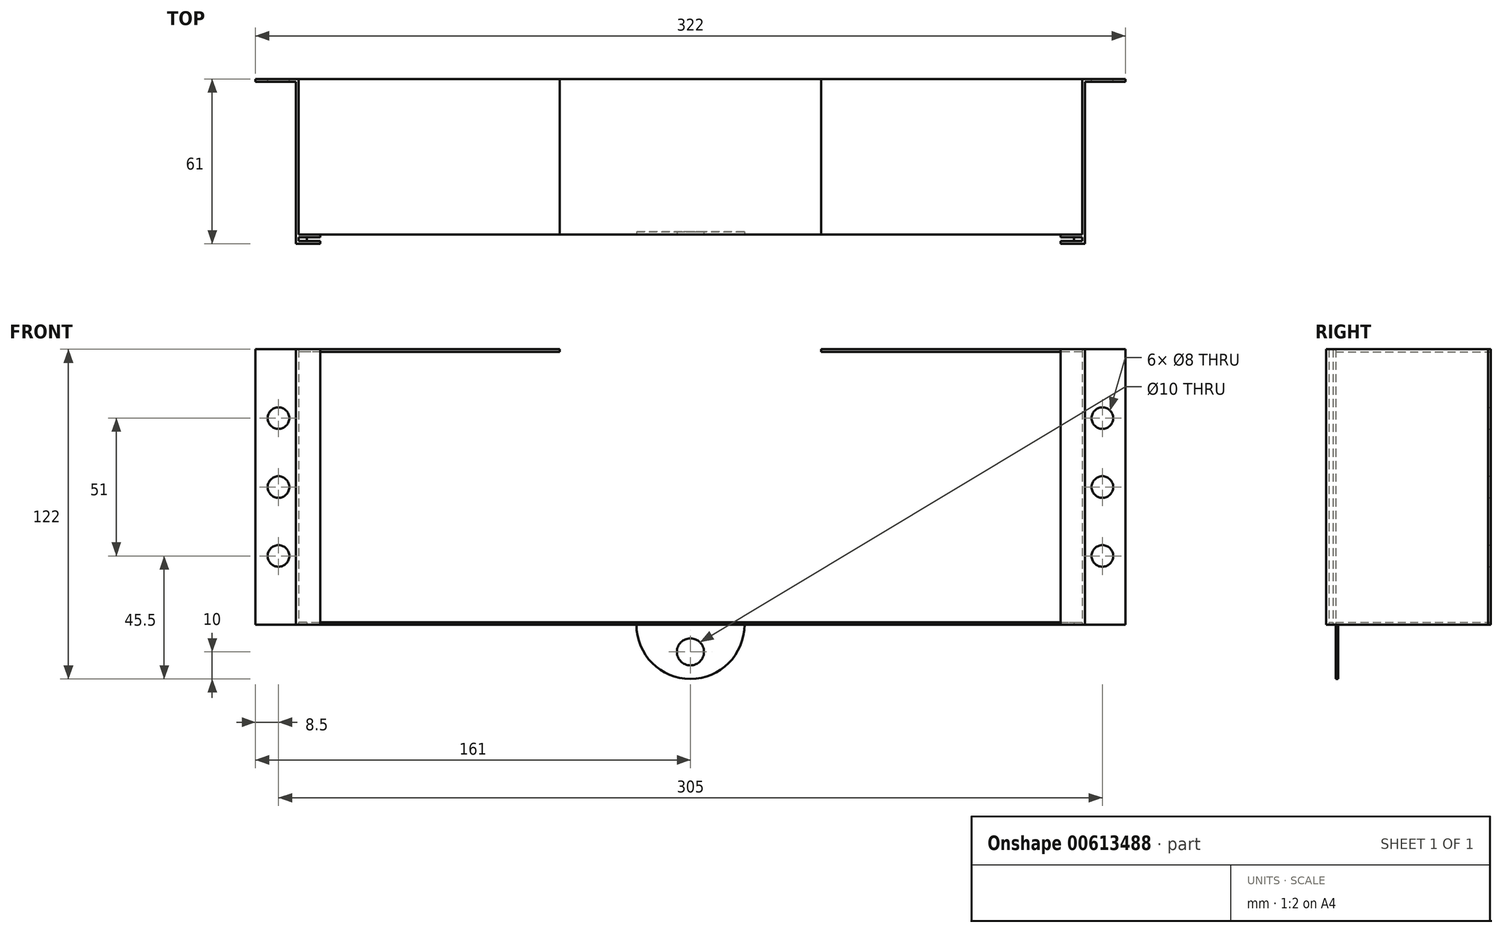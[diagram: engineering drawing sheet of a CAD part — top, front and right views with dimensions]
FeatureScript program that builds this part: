
annotation { "Feature Type Name" : "Feature", "Feature Type Description" : "" }
export const myFeature = defineFeature(function(context is Context, id is Id, definition is map)
    precondition{}
    {
        {
            var Q0;
            Q0=qCreatedBy(makeId("Top.planeOp"),FACE);
            var sketch = newSketch(context, id + "F0", { "sketchPlane" : qUnion([Q0])});
            skLineSegment(sketch, "E0", {"start": v(-146, 0) * mm, "end": v(-146, 60) * mm});
            skLineSegment(sketch, "E1", {"start": v(-146, 60) * mm, "end": v(-161, 60) * mm});
            skLineSegment(sketch, "E2", {"start": v(-161, 60) * mm, "end": v(-161, 61) * mm});
            skLineSegment(sketch, "E3", {"start": v(-161, 61) * mm, "end": v(-145, 61) * mm});
            skLineSegment(sketch, "E4", {"start": v(-145, 61) * mm, "end": v(-145, 3.5) * mm});
            skLineSegment(sketch, "E5", {"start": v(-145, 3.5) * mm, "end": v(-137, 3.5) * mm});
            skLineSegment(sketch, "E6", {"start": v(-137, 3.5) * mm, "end": v(-137, 2.5) * mm});
            skLineSegment(sketch, "E7", {"start": v(-137, 2.5) * mm, "end": v(-145, 2.5) * mm});
            skLineSegment(sketch, "E8", {"start": v(-146, 0) * mm, "end": v(-137, 0) * mm});
            skLineSegment(sketch, "E9", {"start": v(-137, 0) * mm, "end": v(-137, 1) * mm});
            skLineSegment(sketch, "E10", {"start": v(-137, 1) * mm, "end": v(-145, 1) * mm});
            skLineSegment(sketch, "E11", {"start": v(-145, 2.5) * mm, "end": v(-145, 1) * mm});
            skLineSegment(sketch, "E12.MirrorCS", {"start": v(137, 0) * mm, "end": v(137, 1) * mm});
            skLineSegment(sketch, "E13.MirrorCS", {"start": v(137, 3.5) * mm, "end": v(137, 2.5) * mm});
            skLineSegment(sketch, "E14.MirrorCS", {"start": v(145, 2.5) * mm, "end": v(145, 1) * mm});
            skLineSegment(sketch, "E15.MirrorCS", {"start": v(161, 60) * mm, "end": v(161, 61) * mm});
            skLineSegment(sketch, "E16.MirrorCS", {"start": v(146, 0) * mm, "end": v(146, 60) * mm});
            skLineSegment(sketch, "E17.MirrorCS", {"start": v(146, 60) * mm, "end": v(161, 60) * mm});
            skLineSegment(sketch, "E18.MirrorCS", {"start": v(146, 0) * mm, "end": v(137, 0) * mm});
            skLineSegment(sketch, "E19.MirrorCS", {"start": v(145, 3.5) * mm, "end": v(137, 3.5) * mm});
            skLineSegment(sketch, "E20.MirrorCS", {"start": v(145, 61) * mm, "end": v(145, 3.5) * mm});
            skLineSegment(sketch, "E21.MirrorCS", {"start": v(137, 1) * mm, "end": v(145, 1) * mm});
            skLineSegment(sketch, "E22.MirrorCS", {"start": v(161, 61) * mm, "end": v(145, 61) * mm});
            skLineSegment(sketch, "E23.MirrorCS", {"start": v(137, 2.5) * mm, "end": v(145, 2.5) * mm});
            skSolve(sketch);
        }
        {
            var Q0;
            Q0 = qSketchRegion(id + "F0", true);
            extrude(context, id + "F1", {"entities" : qUnion([Q0]), "depth" : 102 * mm, "offsetDistance" : 25 * mm});
        }
        {
            var Q0;
            Q0=makeQuery(id+"F1.opExtrude","SWEPT_FACE",FACE,{"disambiguationData":[OSD([sQuery(id+"F0.wireOp",EDGE,"E22.MirrorCS")])]});
            var sketch = newSketch(context, id + "F2", { "sketchPlane" : qUnion([Q0])});
            skLineSegment(sketch, "E24", {"start": v(-145, 0) * mm, "end": v(145, 0) * mm});
            skLineSegment(sketch, "E25", {"start": v(145, 0) * mm, "end": v(145, 1) * mm});
            skLineSegment(sketch, "E26", {"start": v(145, 1) * mm, "end": v(-145, 1) * mm});
            skLineSegment(sketch, "E27", {"start": v(-145, 1) * mm, "end": v(-145, 0) * mm});
            skLineSegment(sketch, "E28", {"start": v(145, 102) * mm, "end": v(-145, 102) * mm});
            skLineSegment(sketch, "E29", {"start": v(-145, 102) * mm, "end": v(-145, 101) * mm});
            skLineSegment(sketch, "E30", {"start": v(-145, 101) * mm, "end": v(145, 101) * mm});
            skLineSegment(sketch, "E31", {"start": v(145, 102) * mm, "end": v(145, 101) * mm});
            skCircle(sketch, "E32", {"center": v(-152.5, 25.5) * mm, "radius": 4 * mm});
            skCircle(sketch, "E33", {"center": v(-152.5, 51) * mm, "radius": 4 * mm});
            skCircle(sketch, "E34", {"center": v(-152.5, 76.5) * mm, "radius": 4 * mm});
            skCircle(sketch, "E35", {"center": v(152.5, 25.5) * mm, "radius": 4 * mm});
            skCircle(sketch, "E36", {"center": v(152.5, 51) * mm, "radius": 4 * mm});
            skCircle(sketch, "E37", {"center": v(152.5, 76.5) * mm, "radius": 4 * mm});
            skSolve(sketch);
        }
        {
            var Q0;
            Q0=makeQuery(id+"F2.imprint","IMPRINT",FACE,{"disambiguationData":[TD([[makeQuery(id+"F2.imprint","IMPRINT",EDGE,{"derivedFrom":sQuery(id+"F2.wireOp",EDGE,"E28")}),1.0]])]});
            var Q1;
            Q1=makeQuery(id+"F2.imprint","IMPRINT",FACE,{"disambiguationData":[TD([[makeQuery(id+"F2.imprint","IMPRINT",EDGE,{"derivedFrom":sQuery(id+"F2.wireOp",EDGE,"E24")}),1.0]])]});
            extrude(context, id + "F3", {"entities" : qUnion([Q0, Q1]), "oppositeDirection" : true, "depth" : 57.5 * mm, "offsetDistance" : 25 * mm});
        }
        {
            var Q0;
            Q0=makeQuery(id+"F2.imprint","IMPRINT",FACE,{"disambiguationData":[TD([[makeQuery(id+"F2.imprint","IMPRINT",EDGE,{"derivedFrom":sQuery(id+"F2.wireOp",EDGE,"E34")}),1.0]])]});
            var Q1;
            Q1=makeQuery(id+"F2.imprint","IMPRINT",FACE,{"disambiguationData":[TD([[makeQuery(id+"F2.imprint","IMPRINT",EDGE,{"derivedFrom":sQuery(id+"F2.wireOp",EDGE,"E33")}),1.0]])]});
            var Q2;
            Q2=makeQuery(id+"F2.imprint","IMPRINT",FACE,{"disambiguationData":[TD([[makeQuery(id+"F2.imprint","IMPRINT",EDGE,{"derivedFrom":sQuery(id+"F2.wireOp",EDGE,"E32")}),1.0]])]});
            var Q3;
            Q3=makeQuery(id+"F2.imprint","IMPRINT",FACE,{"disambiguationData":[TD([[makeQuery(id+"F2.imprint","IMPRINT",EDGE,{"derivedFrom":sQuery(id+"F2.wireOp",EDGE,"E37")}),1.0]])]});
            var Q4;
            Q4=makeQuery(id+"F2.imprint","IMPRINT",FACE,{"disambiguationData":[TD([[makeQuery(id+"F2.imprint","IMPRINT",EDGE,{"derivedFrom":sQuery(id+"F2.wireOp",EDGE,"E36")}),1.0]])]});
            var Q5;
            Q5=makeQuery(id+"F2.imprint","IMPRINT",FACE,{"disambiguationData":[TD([[makeQuery(id+"F2.imprint","IMPRINT",EDGE,{"derivedFrom":sQuery(id+"F2.wireOp",EDGE,"E35")}),1.0]])]});
            var Q6;
            Q6=sQuery(id+"F2.wireOp",EDGE,"E37");
            var Q7;
            Q7=sQuery(id+"F2.wireOp",EDGE,"E36");
            var Q8;
            Q8=sQuery(id+"F2.wireOp",EDGE,"E35");
            var Q9;
            Q9=sQuery(id+"F2.wireOp",EDGE,"E34");
            var Q10;
            Q10=sQuery(id+"F2.wireOp",EDGE,"E33");
            var Q11;
            Q11=sQuery(id+"F2.wireOp",EDGE,"E32");
            extrude(context, id + "F4", {"entities" : qUnion([Q0, Q1, Q2, Q3, Q4, Q5]), "operationType" : NewBodyOperationType.REMOVE, "surfaceEntities" : qUnion([Q6, Q7, Q8, Q9, Q10, Q11]), "endBound" : BoundingType.UP_TO_NEXT, "oppositeDirection" : true, "depth" : 1 * mm, "offsetDistance" : 25 * mm});
        }
        {
            var Q0;
            Q0=makeQuery(id+"F1.opExtrude","CAP_FACE",FACE,{"disambiguationData":[OSD([sQuery(id+"F0.wireOp",EDGE,"E0"),sQuery(id+"F0.wireOp",EDGE,"E1"),sQuery(id+"F0.wireOp",EDGE,"E2"),sQuery(id+"F0.wireOp",EDGE,"E3"),sQuery(id+"F0.wireOp",EDGE,"E4"),sQuery(id+"F0.wireOp",EDGE,"E5"),sQuery(id+"F0.wireOp",EDGE,"E6"),sQuery(id+"F0.wireOp",EDGE,"E7"),sQuery(id+"F0.wireOp",EDGE,"E8"),sQuery(id+"F0.wireOp",EDGE,"E9"),sQuery(id+"F0.wireOp",EDGE,"E10"),sQuery(id+"F0.wireOp",EDGE,"E11")])],"isStart":true});
            var sketch = newSketch(context, id + "F5", { "sketchPlane" : qUnion([Q0])});
            skLineSegment(sketch, "E38", {"start": v(-145, -1) * mm, "end": v(-145, -2.5) * mm});
            skLineSegment(sketch, "E39", {"start": v(-145, -2.5) * mm, "end": v(-142, -2.5) * mm});
            skLineSegment(sketch, "E40", {"start": v(-142, -2.5) * mm, "end": v(-142, -1) * mm});
            skLineSegment(sketch, "E41", {"start": v(-142, -1) * mm, "end": v(-145, -1) * mm});
            skLineSegment(sketch, "E42.MirrorCS", {"start": v(145, -1) * mm, "end": v(145, -2.5) * mm});
            skLineSegment(sketch, "E43.MirrorCS", {"start": v(145, -2.5) * mm, "end": v(142, -2.5) * mm});
            skLineSegment(sketch, "E44.MirrorCS", {"start": v(142, -2.5) * mm, "end": v(142, -1) * mm});
            skLineSegment(sketch, "E45.MirrorCS", {"start": v(142, -1) * mm, "end": v(145, -1) * mm});
            skSolve(sketch);
        }
        {
            var Q0;
            Q0 = qSketchRegion(id + "F5", true);
            extrude(context, id + "F6", {"entities" : qUnion([Q0]), "oppositeDirection" : true, "depth" : 1 * mm, "offsetDistance" : 25 * mm});
        }
        {
            var Q0;
            Q0=makeQuery(id+"F3.opExtrude","CAP_FACE",FACE,{"disambiguationData":[OSD([sQuery(id+"F2.wireOp",EDGE,"E24"),sQuery(id+"F2.wireOp",EDGE,"E25"),sQuery(id+"F2.wireOp",EDGE,"E26"),sQuery(id+"F2.wireOp",EDGE,"E27")])],"isStart":false});
            var sketch = newSketch(context, id + "F7", { "sketchPlane" : qUnion([Q0])});
            skArc(sketch, "E46", {"start": v(-20, 0) * mm, "mid": v(0, -20) * mm, "end": v(20, 0) * mm});
            skCircle(sketch, "E47", {"center": v(0, -10) * mm, "radius": 5 * mm});
            skLineSegment(sketch, "E48", {"start": v(-20, 0) * mm, "end": v(20, 0) * mm});
            skSolve(sketch);
        }
        {
            var Q0;
            Q0 = qSketchRegion(id + "F7", true);
            extrude(context, id + "F8", {"entities" : qUnion([Q0]), "oppositeDirection" : true, "depth" : 1 * mm, "offsetDistance" : 25 * mm});
        }
        {
            var Q0;
            Q0=qCreatedBy(makeId("Front.planeOp"),FACE);
            var sketch = newSketch(context, id + "F9", { "sketchPlane" : qUnion([Q0])});
            skLineSegment(sketch, "E49", {"start": v(-172.65, 51) * mm, "end": v(174.22, 51) * mm, "construction": true});
            skLineSegment(sketch, "E50", {"start": v(-181.22, 126) * mm, "end": v(176.08, 126) * mm, "construction": true});
            skLineSegment(sketch, "E51", {"start": v(-48.43, 102.1) * mm, "end": v(-48.43, 100.32) * mm});
            skLineSegment(sketch, "E52", {"start": v(-48.43, 100.32) * mm, "end": v(48.39, 100.32) * mm});
            skLineSegment(sketch, "E53", {"start": v(48.39, 100.32) * mm, "end": v(48.39, 102.02) * mm});
            skLineSegment(sketch, "E54", {"start": v(48.39, 102.02) * mm, "end": v(-48.43, 102.1) * mm});
            skPoint(sketch, "E55.center.orphan", {"position": v(0, 126) * mm});
            skSolve(sketch);
        }
        {
            var Q0;
            Q0 = qSketchRegion(id + "F9", true);
            extrude(context, id + "F10", {"entities" : qUnion([Q0]), "operationType" : NewBodyOperationType.REMOVE, "oppositeDirection" : true, "depth" : 61 * mm, "offsetDistance" : 25 * mm});
        }
    });
